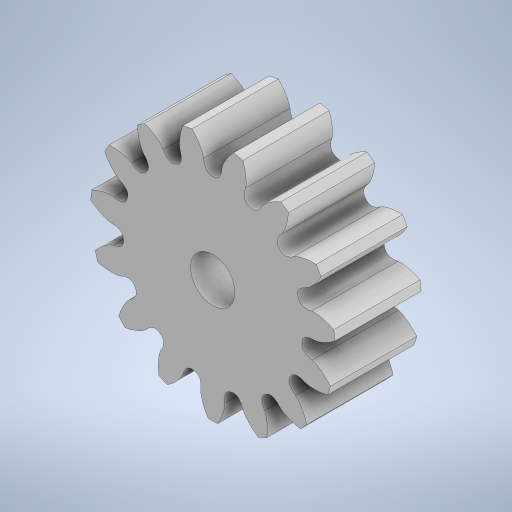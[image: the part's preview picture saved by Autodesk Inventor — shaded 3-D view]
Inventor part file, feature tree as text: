
AUTODESK INVENTOR PART (.ipt)
format: ipt  version: 2023 (Build 270158000, 158)  size: 394,752 bytes
history: native  units: mm
features: sketch x2, extrude x2, pattern_circular x1, hole x1
ambient origin geometry x8: Origin, YZ Plane, XZ Plane, XY Plane, X Axis, Y Axis, Z Axis, Center Point
bodies: Solid1 (feature_tree)
feature tree (6):
  sketch  "Sketch1"  dims[d0=12.0mm d1=0.0mm]
  extrude  "Extrusion1"  TaperAngle=0.0deg  [1 undecoded]
  extrude  "Extrusion2"  Depth=150.0mm TaperAngle=360.0deg
  pattern_circular  "Circular Pattern2"  [2 undecoded]
  hole  "Hole1"  [1 undecoded]
  sketch  "Sketch2"  dims[d2=0.0mm d3=0.0mm d7=150.0mm d8=360.0deg d10=6.171mm d11=6.0mm d12=8.0mm d13=2.0mm d14=90.0deg d15=8.0mm d16=20.594885mm]
note: 4 required parameter values undecoded (feature->parameter linkage not recoverable at this tier; creation-order binding heuristic only, values carry confidence <= 0.55)
